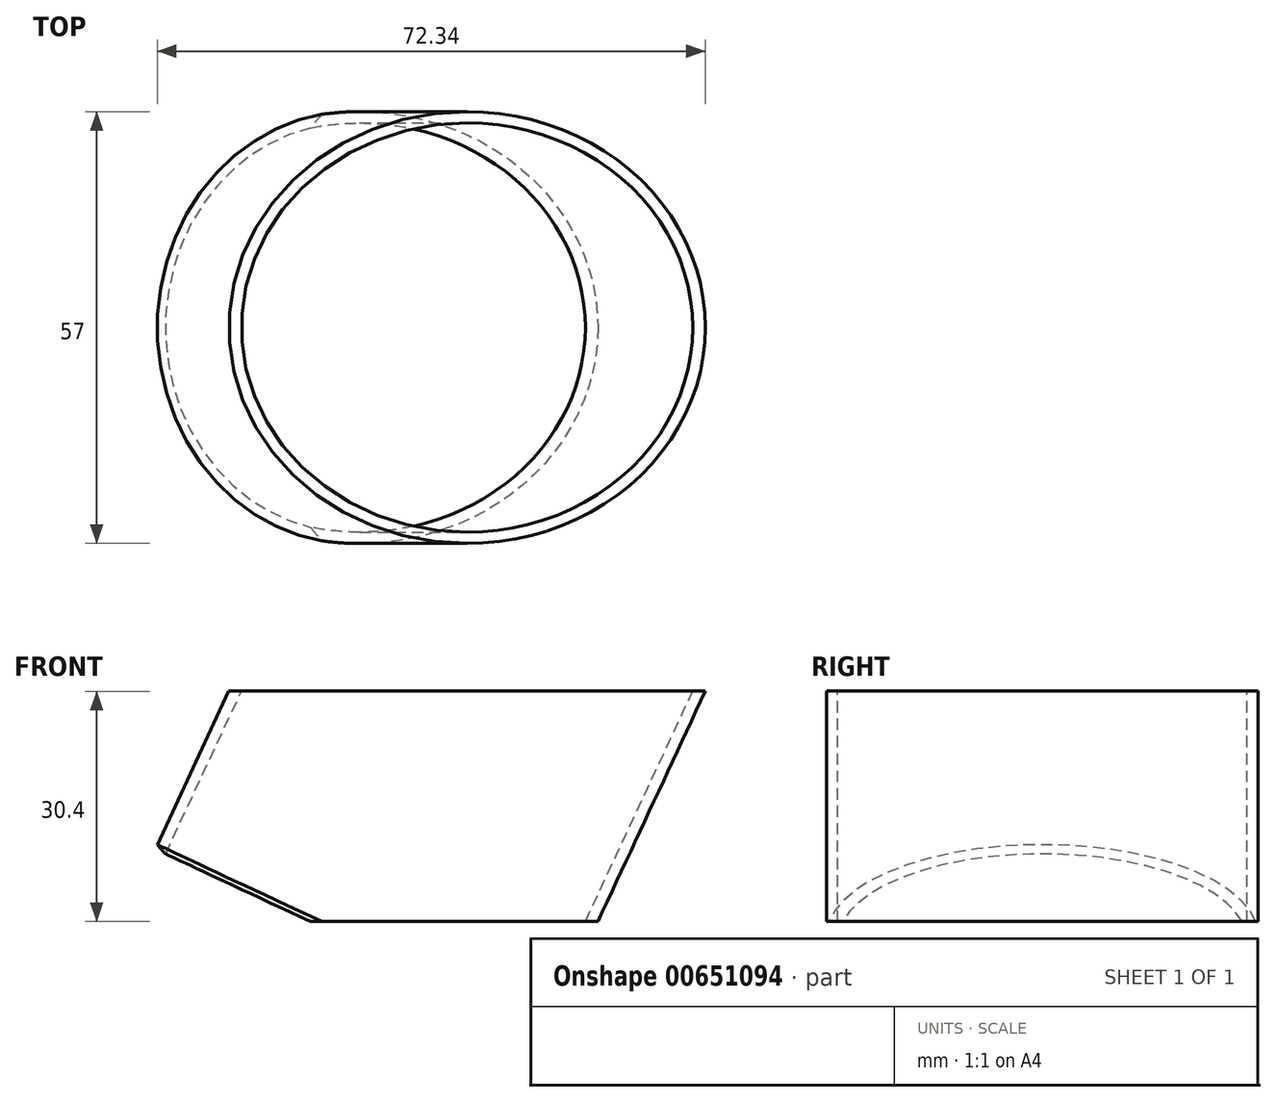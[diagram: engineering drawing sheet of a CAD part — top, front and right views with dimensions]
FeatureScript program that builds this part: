
annotation { "Feature Type Name" : "Feature", "Feature Type Description" : "" }
export const myFeature = defineFeature(function(context is Context, id is Id, definition is map)
    precondition{}
    {
        {
            var Q0;
            Q0=qCreatedBy(makeId("Front.planeOp"),FACE);
            var sketch = newSketch(context, id + "F0", { "sketchPlane" : qUnion([Q0])});
            skLineSegment(sketch, "E0", {"start": v(-115, 22.43) * mm, "end": v(15.5, -38.43) * mm});
            skLineSegment(sketch, "E1", {"start": v(15.5, -38.43) * mm, "end": v(91.58, 124.7) * mm});
            skLineSegment(sketch, "E2", {"start": v(91.58, 124.7) * mm, "end": v(-38.93, 185.56) * mm});
            skLineSegment(sketch, "E3", {"start": v(-38.93, 185.56) * mm, "end": v(-115, 22.43) * mm});
            skLineSegment(sketch, "E4", {"start": v(-84.57, 87.68) * mm, "end": v(45.94, 26.83) * mm});
            skLineSegment(sketch, "E5", {"start": v(26.33, 155.14) * mm, "end": v(-49.75, -8) * mm});
            skEllipticalArc(sketch, "E6", {});
            skEllipticalArc(sketch, "E7", {});
            skLineSegment(sketch, "E8", {"start": v(-56.73, -2.53) * mm, "end": v(-48.9, -6.19) * mm});
            skLineSegment(sketch, "E9", {"start": v(44.12, 27.67) * mm, "end": v(40.47, 19.84) * mm});
            skLineSegment(sketch, "E10", {"start": v(25.48, 153.32) * mm, "end": v(33.31, 149.67) * mm});
            skEllipticalArc(sketch, "E11", {});
            skLineSegment(sketch, "E12", {"start": v(-64.92, 23.35) * mm, "end": v(-15.98, 0.53) * mm});
            skLineSegment(sketch, "E13", {"start": v(-15.98, 0.53) * mm, "end": v(-1.19, 32.25) * mm});
            skLineSegment(sketch, "E14", {"start": v(-1.19, 32.25) * mm, "end": v(-50.13, 55.07) * mm});
            skLineSegment(sketch, "E15", {"start": v(-50.13, 55.07) * mm, "end": v(-64.92, 23.35) * mm});
            skLineSegment(sketch, "E16", {"start": v(-50.13, 55.07) * mm, "end": v(-51.49, 55.7) * mm});
            skLineSegment(sketch, "E17", {"start": v(-51.49, 55.7) * mm, "end": v(-66.28, 23.98) * mm});
            skLineSegment(sketch, "E18", {"start": v(-66.28, 23.98) * mm, "end": v(-64.92, 23.35) * mm});
            skLineSegment(sketch, "E19", {"start": v(-1.19, 32.25) * mm, "end": v(0.17, 31.61) * mm});
            skLineSegment(sketch, "E20", {"start": v(0.17, 31.61) * mm, "end": v(-14.62, -0.1) * mm});
            skLineSegment(sketch, "E21", {"start": v(-14.62, -0.1) * mm, "end": v(-15.98, 0.53) * mm});
            skLineSegment(sketch, "E22", {"start": v(-38.9, 22.68) * mm, "end": v(-38.9, -9.95) * mm});
            skLineSegment(sketch, "E23", {"start": v(-14.62, -0.1) * mm, "end": v(-20.5, -12.74) * mm});
            skLineSegment(sketch, "E24", {"start": v(-15.98, 0.53) * mm, "end": v(-22.16, -12.74) * mm});
            skLineSegment(sketch, "E25", {"start": v(-64.92, 23.35) * mm, "end": v(-71.08, 10.13) * mm});
            skLineSegment(sketch, "E26", {"start": v(-66.28, 23.98) * mm, "end": v(-72.17, 11.35) * mm});
            const initialGuessF0  = {"E6": [-0.01931732448803084, 0.05725416066663877, -0.4226182617406995, -0.90630778703665, 0.072, 0.072, 4.71238898038469, 1.5707963267948966], "E7": [-0.01931732448803084, 0.05725416066663877, 0.4226182617406995, 0.9063077870366499, 0.108, 0.072, 4.71238898038469, 1.5707963267948966], "E7": [-0.01931732448803084, 0.05725416066663877, 0.4226182617406995, 0.9063077870366499, 0.106, 0.07, 4.71238898038469, 1.5707963267948968], "E11": [-0.01931732448803084, 0.05725416066663877, -0.4226182617406995, -0.9063077870366499, 0.07, 0.07, 4.71238898038469, 1.5707963267948966]};
            skSetInitialGuess(sketch, initialGuessF0);
            skSolve(sketch);
        }
        {
            var Q0;
            {var subQ3=sQuery(id+"F0.wireOp",EDGE,"E7");var subQ5=sQuery(id+"F0.wireOp",EDGE,"E5");var subQ7=makeQuery(id+"F0.imprint","INTERSECT",VERTEX,{"derivedFrom":[subQ5,subQ3]});Q0=makeQuery(id+"F0.imprint","IMPRINT",FACE,{"disambiguationData":[TD([[makeQuery(id+"F0.imprint","IMPRINT",EDGE,{"disambiguationData":[TD([[subQ7,1.0]])],"derivedFrom":subQ5}),1.0]])]});}
            var Q1;
            {var subQ0=sQuery(id+"F0.wireOp",EDGE,"E11");var subQ1=sQuery(id+"F0.wireOp",EDGE,"E5");var subQ2=makeQuery(id+"F0.imprint","INTERSECT",VERTEX,{"derivedFrom":[subQ1,subQ0]});Q1=makeQuery(id+"F0.imprint","IMPRINT",FACE,{"disambiguationData":[TD([[makeQuery(id+"F0.imprint","IMPRINT",EDGE,{"disambiguationData":[TD([[subQ2,-1.0]])],"derivedFrom":subQ0}),-1.0]])]});}
            var Q2;
            Q2=makeQuery(id+"F0.imprint","IMPRINT",FACE,{"disambiguationData":[TD([[makeQuery(id+"F0.imprint","IMPRINT",EDGE,{"derivedFrom":sQuery(id+"F0.wireOp",EDGE,"E13")}),-1.0]])]});
            var Q3;
            Q3=makeQuery(id+"F0.imprint","IMPRINT",FACE,{"disambiguationData":[TD([[makeQuery(id+"F0.imprint","IMPRINT",EDGE,{"derivedFrom":sQuery(id+"F0.wireOp",EDGE,"E21")}),1.0]])]});
            var Q4;
            Q4=sQuery(id+"F0.wireOp",EDGE,"E5");
            revolve(context, id + "F1", {"entities" : qUnion([Q0, Q1, Q2, Q3]), "axis" : qUnion([Q4]), "revolveType" : RevolveType.FULL});
        }
        {
            var Q0;
            Q0=qCreatedBy(makeId("Front.planeOp"),FACE);
            var sketch = newSketch(context, id + "F2", { "sketchPlane" : qUnion([Q0])});
            skLineSegment(sketch, "E27.bottom", {"start": v(-100, 0) * mm, "end": v(100, 0) * mm});
            skLineSegment(sketch, "E27.top", {"start": v(-100, -20) * mm, "end": v(100, -20) * mm});
            skLineSegment(sketch, "E27.left", {"start": v(-100, 0) * mm, "end": v(-100, -20) * mm});
            skLineSegment(sketch, "E27.right", {"start": v(100, 0) * mm, "end": v(100, -20) * mm});
            skLineSegment(sketch, "E28.bottom", {"start": v(-109.32, 65) * mm, "end": v(90.68, 65) * mm});
            skLineSegment(sketch, "E28.top", {"start": v(-109.32, 165) * mm, "end": v(90.68, 165) * mm});
            skLineSegment(sketch, "E28.left", {"start": v(-109.32, 65) * mm, "end": v(-109.32, 165) * mm});
            skLineSegment(sketch, "E28.right", {"start": v(90.68, 65) * mm, "end": v(90.68, 165) * mm});
            skLineSegment(sketch, "E29.bottom", {"start": v(-74.83, 56.61) * mm, "end": v(0.17, 56.61) * mm});
            skLineSegment(sketch, "E29.top", {"start": v(-74.83, 31.61) * mm, "end": v(0.17, 31.61) * mm});
            skLineSegment(sketch, "E29.left", {"start": v(-74.83, 56.61) * mm, "end": v(-74.83, 31.61) * mm});
            skLineSegment(sketch, "E29.right", {"start": v(0.17, 56.61) * mm, "end": v(0.17, 31.61) * mm});
            skSolve(sketch);
        }
        {
            var Q0;
            Q0=makeQuery(id+"F2.imprint","IMPRINT",FACE,{"disambiguationData":[TD([[makeQuery(id+"F2.imprint","IMPRINT",EDGE,{"derivedFrom":sQuery(id+"F2.wireOp",EDGE,"E28.bottom")}),1.0]])]});
            var Q1;
            Q1=makeQuery(id+"F2.imprint","IMPRINT",FACE,{"disambiguationData":[TD([[makeQuery(id+"F2.imprint","IMPRINT",EDGE,{"derivedFrom":sQuery(id+"F2.wireOp",EDGE,"E27.bottom")}),-1.0]])]});
            extrude(context, id + "F3", {"entities" : qUnion([Q0, Q1]), "operationType" : NewBodyOperationType.REMOVE, "endBound" : BoundingType.SYMMETRIC, "oppositeDirection" : true, "depth" : 200 * mm, "offsetDistance" : 25 * mm});
        }
        {
            var Q0;
            Q0=makeQuery(id+"F3.boolean.opBoolean","COPY",FACE,{"derivedFrom":makeQuery(id+"F3.opExtrude","SWEPT_FACE",FACE,{"disambiguationData":[OSD([sQuery(id+"F2.wireOp",EDGE,"E27.bottom")])]})});
            var sketch = newSketch(context, id + "F4", { "sketchPlane" : qUnion([Q0])});
            skSolve(sketch);
        }
        {
            var Q0;
            {var subQ0=makeQuery(id+"F3.opExtrude","SWEPT_FACE",FACE,{"disambiguationData":[OSD([sQuery(id+"F2.wireOp",EDGE,"E27.bottom")])]});var subQ2=sQuery(id+"F0.wireOp",EDGE,"O2z92r0F-cPKd-4sDV-DUec-xsLxt2DDbrHl");Q0=makeQuery(id+"F4.imprint","IMPRINT",FACE,{"disambiguationData":[TD([[makeQuery(id+"F4.imprint","IMPRINT",EDGE,{"derivedFrom":makeQuery(id+"F3.boolean.opBoolean","INTERSECT",EDGE,{"derivedFrom":[makeQuery(id+"F1.opRevolve","SWEPT_FACE",FACE,{"disambiguationData":[OSD([subQ2])]}),subQ0]})}),-1.0]])]});}
            var Q1;
            {var subQ0=makeQuery(id+"F3.opExtrude","SWEPT_FACE",FACE,{"disambiguationData":[OSD([sQuery(id+"F2.wireOp",EDGE,"E27.bottom")])]});var subQ2=sQuery(id+"F0.wireOp",EDGE,"888Vat3U-CfOJ-MNbQ-31ce-unUiXKyLYnsl");Q1=makeQuery(id+"F4.imprint","IMPRINT",FACE,{"disambiguationData":[TD([[makeQuery(id+"F4.imprint","IMPRINT",EDGE,{"derivedFrom":makeQuery(id+"F3.boolean.opBoolean","INTERSECT",EDGE,{"derivedFrom":[makeQuery(id+"F1.opRevolve","SWEPT_FACE",FACE,{"disambiguationData":[OSD([subQ2])]}),subQ0]})}),1.0]])]});}
            var Q2;
            {var subQ0=makeQuery(id+"F3.opExtrude","SWEPT_FACE",FACE,{"disambiguationData":[OSD([sQuery(id+"F2.wireOp",EDGE,"E27.bottom")])]});Q2=makeQuery(id+"F4.imprint","IMPRINT",FACE,{"disambiguationData":[TD([[makeQuery(id+"F4.imprint","IMPRINT",EDGE,{"derivedFrom":makeQuery(id+"F3.boolean.opBoolean","INTERSECT",EDGE,{"derivedFrom":[makeQuery(id+"F1.opRevolve","SWEPT_FACE",FACE,{"disambiguationData":[OSD([sQuery(id+"F0.wireOp",EDGE,"E6")])]}),subQ0]})}),1.0]])]});}
            var Q3;
            {var subQ0=makeQuery(id+"F3.opExtrude","SWEPT_FACE",FACE,{"disambiguationData":[OSD([sQuery(id+"F2.wireOp",EDGE,"E27.bottom")])]});var subQ1=sQuery(id+"F0.wireOp",EDGE,"E4I1S2jE-wphf-GyGp-aZi5-idjyPRKCvlRG");Q3=makeQuery(id+"F4.imprint","IMPRINT",FACE,{"disambiguationData":[TD([[makeQuery(id+"F4.imprint","IMPRINT",EDGE,{"derivedFrom":makeQuery(id+"F3.boolean.opBoolean","INTERSECT",EDGE,{"derivedFrom":[makeQuery(id+"F1.opRevolve","SWEPT_FACE",FACE,{"disambiguationData":[OSD([subQ1])]}),subQ0]})}),-1.0]])]});}
            extrude(context, id + "F5", {"entities" : qUnion([Q0, Q1, Q2, Q3]), "operationType" : NewBodyOperationType.ADD, "oppositeDirection" : true, "depth" : 1.2 * mm, "offsetDistance" : 25 * mm, "hasDraft" : true, "draftAngle" : 48 * degree});
        }
        {
            var Q0;
            {var subQ1=sQuery(id+"F2.wireOp",EDGE,"E29.top");Q0=makeQuery(id+"F2.imprint","IMPRINT",FACE,{"disambiguationData":[TD([[makeQuery(id+"F2.imprint","IMPRINT",EDGE,{"derivedFrom":subQ1}),1.0]])]});}
            extrude(context, id + "F6", {"entities" : qUnion([Q0]), "operationType" : NewBodyOperationType.REMOVE, "endBound" : BoundingType.SYMMETRIC, "oppositeDirection" : true, "depth" : 70 * mm, "offsetDistance" : 25 * mm});
        }
        {
            var Q0;
            {var subQ0=sQuery(id+"F0.wireOp",EDGE,"E11");var subQ9=makeQuery(id+"F0.imprint","INTERSECT",VERTEX,{"derivedFrom":[subQ0,sQuery(id+"F0.wireOp",EDGE,"E25")]});Q0=makeQuery(id+"F0.imprint","IMPRINT",FACE,{"disambiguationData":[TD([[makeQuery(id+"F0.imprint","IMPRINT",EDGE,{"disambiguationData":[TD([[subQ9,1.0]])],"derivedFrom":subQ0}),-1.0]])]});}
            var Q1;
            {var subQ3=sQuery(id+"F0.wireOp",EDGE,"E7");var subQ5=sQuery(id+"F0.wireOp",EDGE,"E5");var subQ6=makeQuery(id+"F0.imprint","INTERSECT",VERTEX,{"derivedFrom":[subQ5,subQ3]});Q1=makeQuery(id+"F0.imprint","IMPRINT",FACE,{"disambiguationData":[TD([[makeQuery(id+"F0.imprint","IMPRINT",EDGE,{"disambiguationData":[TD([[subQ6,1.0]])],"derivedFrom":subQ5}),-1.0]])]});}
            var Q2;
            Q2=sQuery(id+"F0.wireOp",EDGE,"E5");
            revolve(context, id + "F7", {"operationType" : NewBodyOperationType.REMOVE, "entities" : qUnion([Q0, Q1]), "axis" : qUnion([Q2]), "revolveType" : RevolveType.FULL, "oppositeDirection" : true});
        }
        {
            var Q0;
            Q0=qCreatedBy(makeId("Front.planeOp"),FACE);
            var sketch = newSketch(context, id + "F8", { "sketchPlane" : qUnion([Q0])});
            skLineSegment(sketch, "E30.bottom", {"start": v(-67.07, 1.2) * mm, "end": v(29, 1.2) * mm});
            skLineSegment(sketch, "E30.top", {"start": v(-67.07, -4.05) * mm, "end": v(29, -4.05) * mm});
            skLineSegment(sketch, "E30.left", {"start": v(-67.07, 1.2) * mm, "end": v(-67.07, -4.05) * mm});
            skLineSegment(sketch, "E30.right", {"start": v(29, 1.2) * mm, "end": v(29, -4.05) * mm});
            skSolve(sketch);
        }
        {
            var Q0;
            Q0=makeQuery(id+"F8.imprint","IMPRINT",FACE,{"disambiguationData":[TD([[makeQuery(id+"F8.imprint","IMPRINT",EDGE,{"derivedFrom":sQuery(id+"F8.wireOp",EDGE,"E30.bottom")}),-1.0]])]});
            extrude(context, id + "F9", {"entities" : qUnion([Q0]), "operationType" : NewBodyOperationType.REMOVE, "endBound" : BoundingType.SYMMETRIC, "oppositeDirection" : true, "depth" : 100 * mm, "offsetDistance" : 25 * mm});
        }
    });
